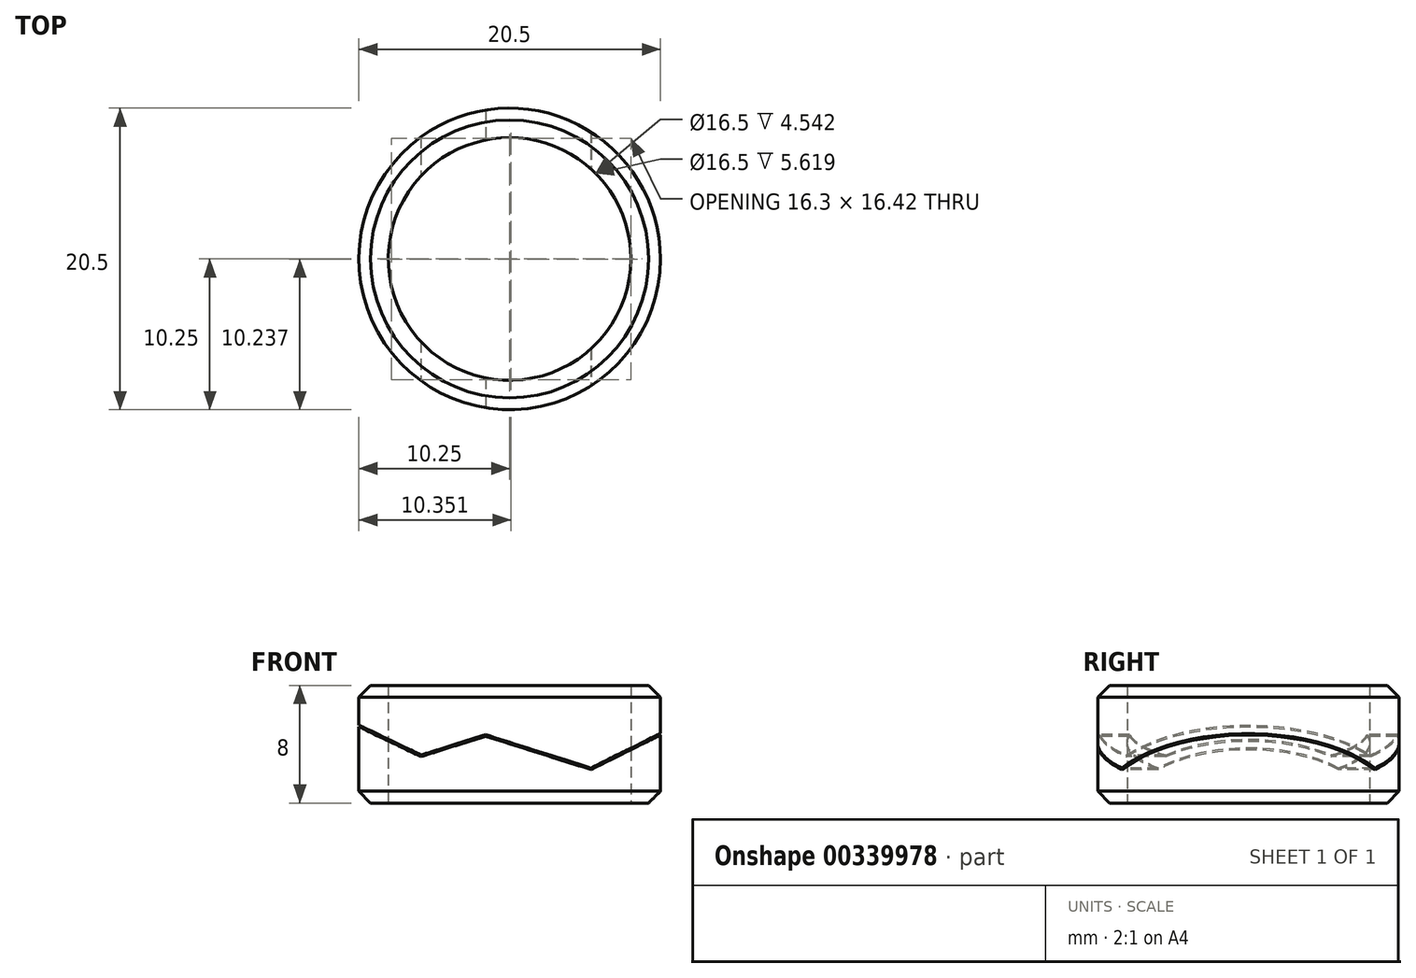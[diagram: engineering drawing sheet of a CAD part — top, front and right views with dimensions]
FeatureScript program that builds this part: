
annotation { "Feature Type Name" : "Feature", "Feature Type Description" : "" }
export const myFeature = defineFeature(function(context is Context, id is Id, definition is map)
    precondition{}
    {
        {
            var Q0;
            Q0=qCreatedBy(makeId("Top.planeOp"),FACE);
            var sketch = newSketch(context, id + "F0", { "sketchPlane" : qUnion([Q0])});
            skCircle(sketch, "E0", {"center": v(0, 0) * mm, "radius": 8.25 * mm});
            skCircle(sketch, "E1", {"center": v(0, 0) * mm, "radius": 10.25 * mm});
            skSolve(sketch);
        }
        {
            var Q0;
            Q0 = qSketchRegion(id + "F0", true);
            extrude(context, id + "F1", {"entities" : qUnion([Q0]), "depth" : 8 * mm});
        }
        {
            var Q0;
            Q0=qCreatedBy(makeId("Front.planeOp"),FACE);
            var sketch = newSketch(context, id + "F2", { "sketchPlane" : qUnion([Q0])});
            skLineSegment(sketch, "E2", {"start": v(-10.25, 0) * mm, "end": v(-10.25, 8) * mm});
            skLineSegment(sketch, "E3", {"start": v(10.25, 9.25) * mm, "end": v(10.25, 0) * mm});
            skLineSegment(sketch, "E4", {"start": v(-10.25, 5.2) * mm, "end": v(-6.03, 3.16) * mm});
            skLineSegment(sketch, "E5", {"start": v(-6.03, 3.16) * mm, "end": v(-1.63, 4.54) * mm});
            skLineSegment(sketch, "E6", {"start": v(-1.63, 4.54) * mm, "end": v(5.54, 2.27) * mm});
            skLineSegment(sketch, "E7", {"start": v(5.54, 2.27) * mm, "end": v(10.25, 4.62) * mm});
            skLineSegment(sketch, "E8.0", {"start": v(5.53, 2.38) * mm, "end": v(9.74, 4.48) * mm});
            skLineSegment(sketch, "E8.1", {"start": v(-1.63, 4.65) * mm, "end": v(5.53, 2.38) * mm});
            skLineSegment(sketch, "E8.2", {"start": v(-6.02, 3.26) * mm, "end": v(-1.63, 4.65) * mm});
            skLineSegment(sketch, "E8.3", {"start": v(-10.9, 5.62) * mm, "end": v(-6.02, 3.26) * mm});
            skLineSegment(sketch, "E9", {"start": v(9.74, 4.48) * mm, "end": v(11.05, 5.13) * mm});
            skSolve(sketch);
        }
        {
            var Q0;
            Q0 = qSketchRegion(id + "F2", true);
            extrude(context, id + "F3", {"entities" : qUnion([Q0]), "operationType" : NewBodyOperationType.REMOVE, "oppositeDirection" : true, "depth" : 25 * mm, "hasSecondDirection" : true, "secondDirectionOppositeDirection" : false, "secondDirectionDepth" : 25 * mm});
        }
        {
            var Q0;
            Q0=makeQuery(id+"F1.opExtrude","CAP_EDGE",EDGE,{"disambiguationData":[OSD([sQuery(id+"F0.wireOp",EDGE,"E1")])],"isStart":false});
            var Q1;
            Q1=makeQuery(id+"F1.opExtrude","CAP_EDGE",EDGE,{"disambiguationData":[OSD([sQuery(id+"F0.wireOp",EDGE,"E1")])],"isStart":true});
            chamfer(context, id + "F4", {"entities" : qUnion([Q0, Q1]), "width" : 0.8 * mm, "tangentPropagation" : true});
        }
    });
